# Revit family: ЭВАН ЭПВН 7,5 кВт
name_source: partatom
category: Оборудование
units: mm (PartAtom-declared; Revit-internal decimal feet)

## family parameters
Всегда вертикально = Да
Классификация = Нет
На основе рабочей плоскости = Да
Общий = Нет
При загрузке вырезать с полостями = Нет
Размер круглого соединителя = Использовать диаметр
Тип детали = Нормальный
Точка расчета площади = Нет

## types (1)
- ЭВАН ЭПВН - 7.5 кВт
    ADSK_Классификация нагрузок = Прочее
    ADSK_Количество фаз = 1
    ADSK_Материал = Сталь
    ADSK_Номинальная мощность = 0 Вт
    ADSK_Размер_Высота = 238 мм
    ADSK_Размер_Длина = 549 мм
    ADSK_Размер_Ширина = 250 мм
    ADSK_Расход теплоносителя = 0.2 м³/ч
    Dn = 16 мм
    База = ЭЛЕКТРИЧЕСКИЙ ТЕПЛОГЕНЕРАТОР (КОТЕЛ)
    Крышка_Видимость = Да
    Максимальная температура теплоносителя, оС = +65
    Материал корпуса = Сталь
    Минимально допустимое давление допустимое на входе в водонагреватель, МПа = 0.02
    Мощность 1-й ступени (по умолчанию) = 0 Вт
    Объем колбы котла, л = 3
    Отметка по умолчанию = 0 мм
    Потребляемая электрическая мощность при максимальной тепловой мощность  в час, кВт/ч = 7.87
    Рабоча зона_Видимость = Да
    Резьба патрубков для подключения трубопроводов теплоносителя = G 1/2
